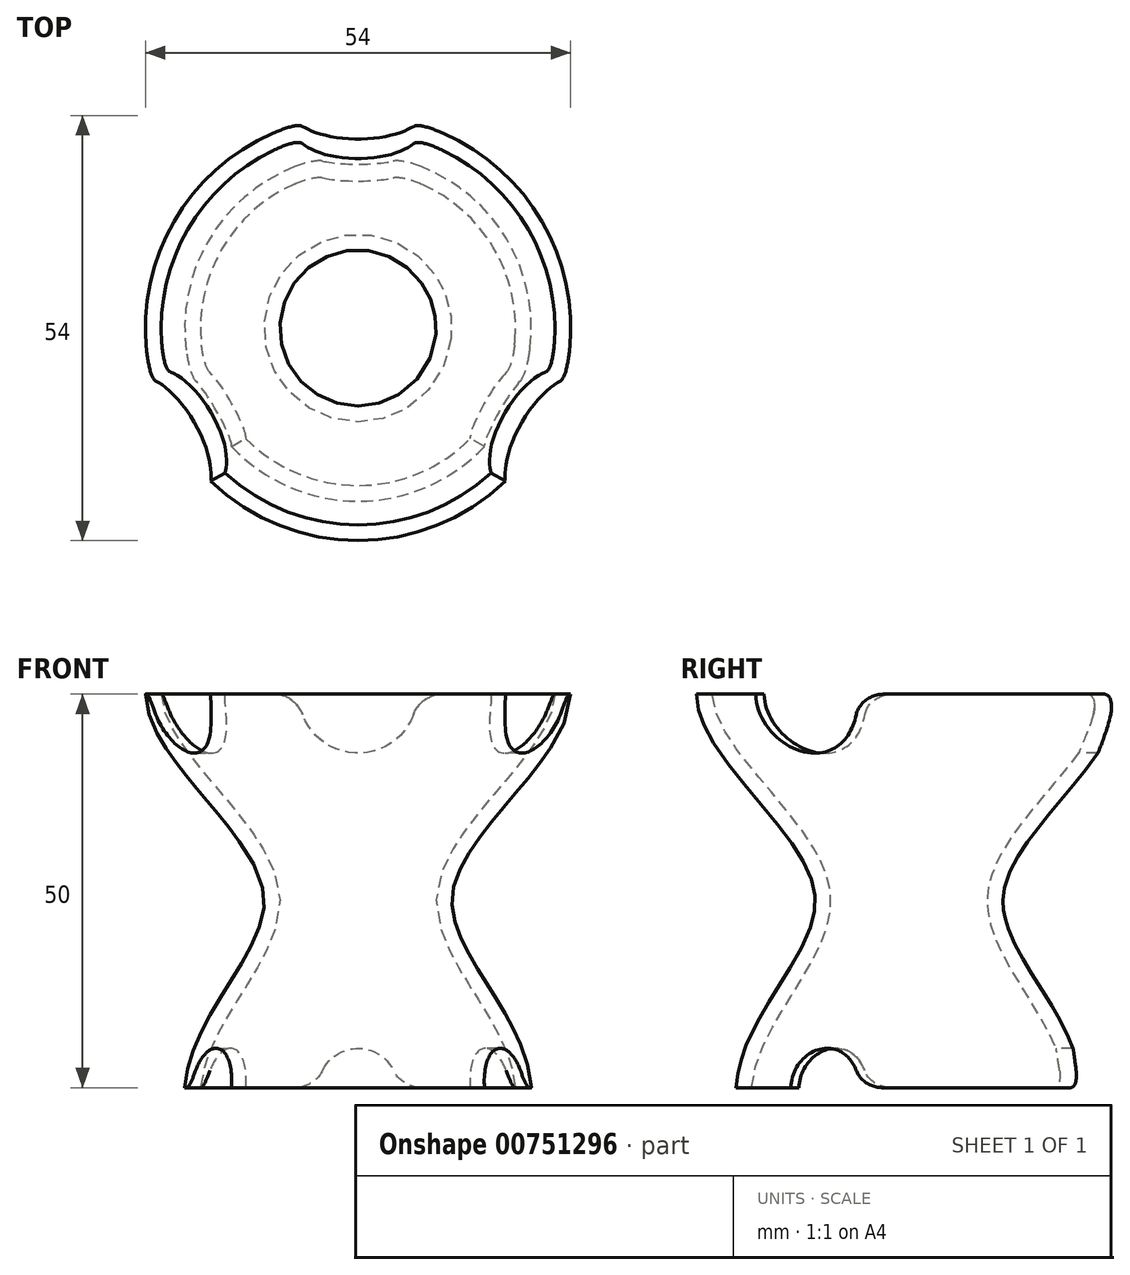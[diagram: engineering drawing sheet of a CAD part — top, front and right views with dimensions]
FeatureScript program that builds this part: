
annotation { "Feature Type Name" : "Feature", "Feature Type Description" : "" }
export const myFeature = defineFeature(function(context is Context, id is Id, definition is map)
    precondition{}
    {
        {
            var Q0;
            Q0=qCreatedBy(makeId("Front.planeOp"),FACE);
            var sketch = newSketch(context, id + "F0", { "sketchPlane" : qUnion([Q0])});
            skLineSegment(sketch, "E0", {"start": v(0, 50) * mm, "end": v(25, 50) * mm});
            skFitSpline(sketch, "E1", {"points": [v(25, 50) * mm, v(10, 25) * mm, v(20, 0) * mm], "startDerivative": vector(-0.97, -42.98) * mm, "endDerivative": vector(4.33, -54.34) * mm});
            skLineSegment(sketch, "E2", {"start": v(20, 0) * mm, "end": v(0, 0) * mm});
            skLineSegment(sketch, "E3", {"start": v(0, 0) * mm, "end": v(0, 50) * mm});
            skLineSegment(sketch, "E4", {"start": v(0, 59.07) * mm, "end": v(0, -15.75) * mm, "construction": true});
            skSolve(sketch);
        }
        {
            var Q0;
            Q0=makeQuery(id+"F0.imprint","IMPRINT",FACE,{"disambiguationData":[TD([[makeQuery(id+"F0.imprint","IMPRINT",EDGE,{"derivedFrom":sQuery(id+"F0.wireOp",EDGE,"E0")}),-1.0]])]});
            var Q1;
            Q1=sQuery(id+"F0.wireOp",EDGE,"E4");
            revolve(context, id + "F1", {"surfaceOperationType" : NewSurfaceOperationType.NEW, "entities" : qUnion([Q0]), "axis" : qUnion([Q1]), "revolveType" : RevolveType.FULL});
        }
        {
            var Q0;
            Q0=makeQuery(id+"F1.opRevolve","SWEPT_FACE",FACE,{"disambiguationData":[OSD([sQuery(id+"F0.wireOp",EDGE,"E0")])]});
            var Q1;
            Q1=makeQuery(id+"F1.opRevolve","SWEPT_FACE",FACE,{"disambiguationData":[OSD([sQuery(id+"F0.wireOp",EDGE,"E2")])]});
            var Q2;
            Q2=makeQuery(id+"F1.opRevolve","SWEPT_BODY",BODY,{"disambiguationData":[OSD([sQuery(id+"F0.wireOp",EDGE,"E0"),sQuery(id+"F0.wireOp",EDGE,"E1"),sQuery(id+"F0.wireOp",EDGE,"E2"),sQuery(id+"F0.wireOp",EDGE,"E3")])]});
            shell(context, id + "F2", {"entities" : qUnion([Q0, Q1]), "parts" : qUnion([Q2]), "thickness" : 2 * mm, "oppositeDirection" : true});
        }
        {
            var Q0;
            Q0=qCreatedBy(makeId("Front.planeOp"),FACE);
            var sketch = newSketch(context, id + "F3", { "sketchPlane" : qUnion([Q0])});
            skLineSegment(sketch, "E5.0", {"start": v(-27, 50) * mm, "end": v(27, 50) * mm});
            skLineSegment(sketch, "E6.0", {"start": v(-22, 0) * mm, "end": v(22, 0) * mm});
            skCircle(sketch, "E7", {"center": v(0, 0) * mm, "radius": 5 * mm});
            skLineSegment(sketch, "E8", {"start": v(0, 0) * mm, "end": v(0, 50) * mm, "construction": true});
            skCircle(sketch, "E9", {"center": v(0, 50) * mm, "radius": 7.5 * mm});
            skSolve(sketch);
        }
        {
            var Q0;
            {var subQ0=sQuery(id+"F3.wireOp",EDGE,"E9");var subQ1=sQuery(id+"F3.wireOp",EDGE,"E5.0");var subQ2=makeQuery(id+"F3.imprint","INTERSECT",VERTEX,{"disambiguationData":[OD(0.0)],"derivedFrom":[subQ1,subQ0]});Q0=makeQuery(id+"F3.imprint","IMPRINT",FACE,{"disambiguationData":[TD([[makeQuery(id+"F3.imprint","IMPRINT",EDGE,{"disambiguationData":[TD([[subQ2,-1.0]])],"derivedFrom":subQ1}),-1.0]])]});}
            var Q1;
            {var subQ0=sQuery(id+"F3.wireOp",EDGE,"E7");var subQ1=sQuery(id+"F3.wireOp",EDGE,"E6.0");var subQ2=makeQuery(id+"F3.imprint","INTERSECT",VERTEX,{"disambiguationData":[OD(0.0)],"derivedFrom":[subQ1,subQ0]});Q1=makeQuery(id+"F3.imprint","IMPRINT",FACE,{"disambiguationData":[TD([[makeQuery(id+"F3.imprint","IMPRINT",EDGE,{"disambiguationData":[TD([[subQ2,-1.0]])],"derivedFrom":subQ1}),1.0]])]});}
            extrude(context, id + "F4", {"entities" : qUnion([Q0, Q1]), "oppositeDirection" : true, "depth" : 60 * mm, "offsetDistance" : 25 * mm});
        }
        {
            var Q0;
            Q0=makeQuery(id+"F4.opExtrude","SWEPT_BODY",BODY,{"disambiguationData":[OSD([sQuery(id+"F3.wireOp",EDGE,"E5.0"),sQuery(id+"F3.wireOp",EDGE,"E9")])]});
            var Q1;
            Q1=makeQuery(id+"F4.opExtrude","SWEPT_BODY",BODY,{"disambiguationData":[OSD([sQuery(id+"F3.wireOp",EDGE,"E6.0"),sQuery(id+"F3.wireOp",EDGE,"E7")])]});
            var Q2;
            Q2=sQuery(id+"F0.wireOp",EDGE,"E4");
            circularPattern(context, id + "F5", {"operationType" : NewBodyOperationType.REMOVE, "entities" : qUnion([Q0, Q1]), "axis" : qUnion([Q2]), "angle" : 360 * degree, "instanceCount" : 3, "equalSpace" : true});
        }
        {
            var Q0;
            {var subQ0=sQuery(id+"F3.wireOp",EDGE,"E9");var subQ1=sQuery(id+"F3.wireOp",EDGE,"E5.0");Q0=makeQuery(id+"F5.boolean.opBoolean","COPY",EDGE,{"derivedFrom":makeQuery(id+"F5.opPattern","COPY",EDGE,{"derivedFrom":makeQuery(id+"F4.opExtrude","SWEPT_EDGE",EDGE,{"disambiguationData":[OSD([subQ1,subQ0]),TDD([makeQuery(id+"F3.imprint","INTERSECT",VERTEX,{"disambiguationData":[OD(1.0)],"derivedFrom":[subQ1,subQ0]})])]}),"instanceName":"1"})});}
            var Q1;
            {var subQ0=sQuery(id+"F3.wireOp",EDGE,"E9");var subQ1=sQuery(id+"F3.wireOp",EDGE,"E5.0");Q1=makeQuery(id+"F5.boolean.opBoolean","COPY",EDGE,{"derivedFrom":makeQuery(id+"F5.opPattern","COPY",EDGE,{"derivedFrom":makeQuery(id+"F4.opExtrude","SWEPT_EDGE",EDGE,{"disambiguationData":[OSD([subQ1,subQ0]),TDD([makeQuery(id+"F3.imprint","INTERSECT",VERTEX,{"disambiguationData":[OD(0.0)],"derivedFrom":[subQ1,subQ0]})])]}),"instanceName":"1"})});}
            var Q2;
            {var subQ0=sQuery(id+"F3.wireOp",EDGE,"E9");var subQ1=sQuery(id+"F3.wireOp",EDGE,"E5.0");Q2=makeQuery(id+"F5.boolean.opBoolean","COPY",EDGE,{"derivedFrom":makeQuery(id+"F5.opPattern","COPY",EDGE,{"derivedFrom":makeQuery(id+"F4.opExtrude","SWEPT_EDGE",EDGE,{"disambiguationData":[OSD([subQ1,subQ0]),TDD([makeQuery(id+"F3.imprint","INTERSECT",VERTEX,{"disambiguationData":[OD(0.0)],"derivedFrom":[subQ1,subQ0]})])]}),"instanceName":"2"})});}
            var Q3;
            {var subQ0=sQuery(id+"F3.wireOp",EDGE,"E9");var subQ1=sQuery(id+"F3.wireOp",EDGE,"E5.0");Q3=makeQuery(id+"F5.boolean.opBoolean","COPY",EDGE,{"derivedFrom":makeQuery(id+"F5.opPattern","COPY",EDGE,{"derivedFrom":makeQuery(id+"F4.opExtrude","SWEPT_EDGE",EDGE,{"disambiguationData":[OSD([subQ1,subQ0]),TDD([makeQuery(id+"F3.imprint","INTERSECT",VERTEX,{"disambiguationData":[OD(1.0)],"derivedFrom":[subQ1,subQ0]})])]}),"instanceName":"2"})});}
            var Q4;
            {var subQ0=sQuery(id+"F3.wireOp",EDGE,"E9");var subQ1=sQuery(id+"F3.wireOp",EDGE,"E5.0");Q4=makeQuery(id+"F5.boolean.opBoolean","COPY",EDGE,{"derivedFrom":makeQuery(id+"F4.opExtrude","SWEPT_EDGE",EDGE,{"disambiguationData":[OSD([subQ1,subQ0]),TDD([makeQuery(id+"F3.imprint","INTERSECT",VERTEX,{"disambiguationData":[OD(0.0)],"derivedFrom":[subQ1,subQ0]})])]})});}
            var Q5;
            {var subQ0=sQuery(id+"F3.wireOp",EDGE,"E9");var subQ1=sQuery(id+"F3.wireOp",EDGE,"E5.0");Q5=makeQuery(id+"F5.boolean.opBoolean","COPY",EDGE,{"derivedFrom":makeQuery(id+"F4.opExtrude","SWEPT_EDGE",EDGE,{"disambiguationData":[OSD([subQ1,subQ0]),TDD([makeQuery(id+"F3.imprint","INTERSECT",VERTEX,{"disambiguationData":[OD(1.0)],"derivedFrom":[subQ1,subQ0]})])]})});}
            var Q6;
            {var subQ0=sQuery(id+"F3.wireOp",EDGE,"E7");var subQ1=sQuery(id+"F3.wireOp",EDGE,"E6.0");Q6=makeQuery(id+"F5.boolean.opBoolean","COPY",EDGE,{"derivedFrom":makeQuery(id+"F4.opExtrude","SWEPT_EDGE",EDGE,{"disambiguationData":[OSD([subQ1,subQ0]),TDD([makeQuery(id+"F3.imprint","INTERSECT",VERTEX,{"disambiguationData":[OD(0.0)],"derivedFrom":[subQ1,subQ0]})])]})});}
            var Q7;
            {var subQ0=sQuery(id+"F3.wireOp",EDGE,"E7");var subQ1=sQuery(id+"F3.wireOp",EDGE,"E6.0");Q7=makeQuery(id+"F5.boolean.opBoolean","COPY",EDGE,{"derivedFrom":makeQuery(id+"F4.opExtrude","SWEPT_EDGE",EDGE,{"disambiguationData":[OSD([subQ1,subQ0]),TDD([makeQuery(id+"F3.imprint","INTERSECT",VERTEX,{"disambiguationData":[OD(1.0)],"derivedFrom":[subQ1,subQ0]})])]})});}
            var Q8;
            {var subQ0=sQuery(id+"F3.wireOp",EDGE,"E7");var subQ1=sQuery(id+"F3.wireOp",EDGE,"E6.0");Q8=makeQuery(id+"F5.boolean.opBoolean","COPY",EDGE,{"derivedFrom":makeQuery(id+"F5.opPattern","COPY",EDGE,{"derivedFrom":makeQuery(id+"F4.opExtrude","SWEPT_EDGE",EDGE,{"disambiguationData":[OSD([subQ1,subQ0]),TDD([makeQuery(id+"F3.imprint","INTERSECT",VERTEX,{"disambiguationData":[OD(0.0)],"derivedFrom":[subQ1,subQ0]})])]}),"instanceName":"1"})});}
            var Q9;
            {var subQ0=sQuery(id+"F3.wireOp",EDGE,"E7");var subQ1=sQuery(id+"F3.wireOp",EDGE,"E6.0");Q9=makeQuery(id+"F5.boolean.opBoolean","COPY",EDGE,{"derivedFrom":makeQuery(id+"F5.opPattern","COPY",EDGE,{"derivedFrom":makeQuery(id+"F4.opExtrude","SWEPT_EDGE",EDGE,{"disambiguationData":[OSD([subQ1,subQ0]),TDD([makeQuery(id+"F3.imprint","INTERSECT",VERTEX,{"disambiguationData":[OD(1.0)],"derivedFrom":[subQ1,subQ0]})])]}),"instanceName":"1"})});}
            var Q10;
            {var subQ0=sQuery(id+"F3.wireOp",EDGE,"E7");var subQ1=sQuery(id+"F3.wireOp",EDGE,"E6.0");Q10=makeQuery(id+"F5.boolean.opBoolean","COPY",EDGE,{"derivedFrom":makeQuery(id+"F5.opPattern","COPY",EDGE,{"derivedFrom":makeQuery(id+"F4.opExtrude","SWEPT_EDGE",EDGE,{"disambiguationData":[OSD([subQ1,subQ0]),TDD([makeQuery(id+"F3.imprint","INTERSECT",VERTEX,{"disambiguationData":[OD(0.0)],"derivedFrom":[subQ1,subQ0]})])]}),"instanceName":"2"})});}
            var Q11;
            {var subQ0=sQuery(id+"F3.wireOp",EDGE,"E7");var subQ1=sQuery(id+"F3.wireOp",EDGE,"E6.0");Q11=makeQuery(id+"F5.boolean.opBoolean","COPY",EDGE,{"derivedFrom":makeQuery(id+"F5.opPattern","COPY",EDGE,{"derivedFrom":makeQuery(id+"F4.opExtrude","SWEPT_EDGE",EDGE,{"disambiguationData":[OSD([subQ1,subQ0]),TDD([makeQuery(id+"F3.imprint","INTERSECT",VERTEX,{"disambiguationData":[OD(1.0)],"derivedFrom":[subQ1,subQ0]})])]}),"instanceName":"2"})});}
            fillet(context, id + "F6", {"entities" : qUnion([Q0, Q1, Q2, Q3, Q4, Q5, Q6, Q7, Q8, Q9, Q10, Q11]), "radius" : 4 * mm, "tangentPropagation" : true, "allowEdgeOverflow" : false});
        }
    });
